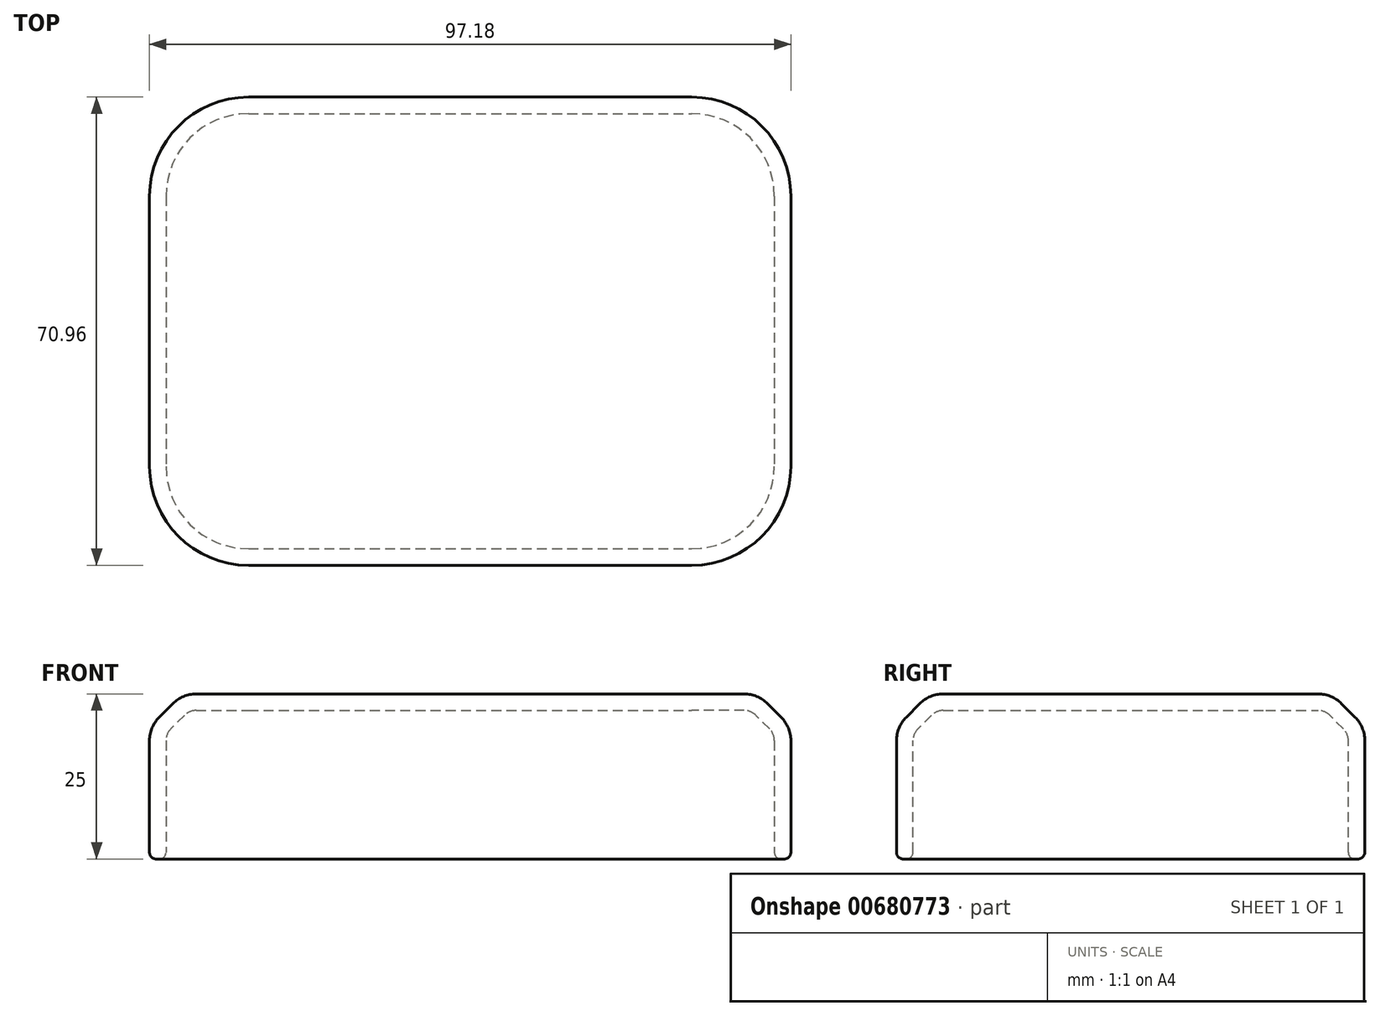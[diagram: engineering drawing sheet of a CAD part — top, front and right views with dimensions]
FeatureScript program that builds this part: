
annotation { "Feature Type Name" : "Feature", "Feature Type Description" : "" }
export const myFeature = defineFeature(function(context is Context, id is Id, definition is map)
    precondition{}
    {
        {
            var Q0;
            Q0=qCreatedBy(makeId("Top.planeOp"),FACE);
            var sketch = newSketch(context, id + "F0", { "sketchPlane" : qUnion([Q0])});
            skLineSegment(sketch, "E0.bottom", {"start": v(-65.06, 47.59) * mm, "end": v(32.12, 47.59) * mm});
            skLineSegment(sketch, "E0.top", {"start": v(-65.06, -23.37) * mm, "end": v(32.12, -23.37) * mm});
            skLineSegment(sketch, "E0.left", {"start": v(-65.06, 47.59) * mm, "end": v(-65.06, -23.37) * mm});
            skLineSegment(sketch, "E0.right", {"start": v(32.12, 47.59) * mm, "end": v(32.12, -23.37) * mm});
            skSolve(sketch);
        }
        {
            var Q0;
            Q0=makeQuery(id+"F0.imprint","IMPRINT",FACE,{"disambiguationData":[TD([[makeQuery(id+"F0.imprint","IMPRINT",EDGE,{"derivedFrom":sQuery(id+"F0.wireOp",EDGE,"E0.bottom")}),-1.0]])]});
            extrude(context, id + "F1", {"entities" : qUnion([Q0]), "depth" : 25 * mm, "offsetDistance" : 25 * mm});
        }
        {
            var Q0;
            Q0=makeQuery(id+"F1.opExtrude","SWEPT_EDGE",EDGE,{"disambiguationData":[OSD([sQuery(id+"F0.wireOp",EDGE,"E0.top"),sQuery(id+"F0.wireOp",EDGE,"E0.left")])]});
            var Q1;
            Q1=makeQuery(id+"F1.opExtrude","SWEPT_EDGE",EDGE,{"disambiguationData":[OSD([sQuery(id+"F0.wireOp",EDGE,"E0.top"),sQuery(id+"F0.wireOp",EDGE,"E0.right")])]});
            var Q2;
            Q2=makeQuery(id+"F1.opExtrude","SWEPT_EDGE",EDGE,{"disambiguationData":[OSD([sQuery(id+"F0.wireOp",EDGE,"E0.bottom"),sQuery(id+"F0.wireOp",EDGE,"E0.right")])]});
            var Q3;
            Q3=makeQuery(id+"F1.opExtrude","SWEPT_EDGE",EDGE,{"disambiguationData":[OSD([sQuery(id+"F0.wireOp",EDGE,"E0.bottom"),sQuery(id+"F0.wireOp",EDGE,"E0.left")])]});
            fillet(context, id + "F2", {"entities" : qUnion([Q0, Q1, Q2, Q3]), "radius" : 15 * mm, "tangentPropagation" : true, "allowEdgeOverflow" : false});
        }
        {
            var Q0;
            Q0=makeQuery(id+"F1.opExtrude","CAP_EDGE",EDGE,{"disambiguationData":[OSD([sQuery(id+"F0.wireOp",EDGE,"E0.left")])],"isStart":false});
            chamfer(context, id + "F3", {"entities" : qUnion([Q0]), "width" : 5 * mm, "tangentPropagation" : true});
        }
        {
            var Q0;
            {var subQ0=sQuery(id+"F0.wireOp",EDGE,"E0.left");Q0=makeQuery(id+"F3.opChamfer","BLEND_EDGE",EDGE,{"blendedFrom":[makeQuery(id+"F1.opExtrude","CAP_EDGE",EDGE,{"disambiguationData":[OSD([subQ0])],"isStart":false}),makeQuery(id+"F1.opExtrude","SWEPT_FACE",FACE,{"disambiguationData":[OSD([subQ0])]})],"blendedInto":[makeQuery(id+"F1.opExtrude","SWEPT_FACE",FACE,{"disambiguationData":[OSD([subQ0])]})]});}
            var Q1;
            {var subQ0=sQuery(id+"F0.wireOp",EDGE,"E0.left");Q1=makeQuery(id+"F3.opChamfer","BLEND_EDGE",EDGE,{"blendedFrom":[makeQuery(id+"F1.opExtrude","CAP_EDGE",EDGE,{"disambiguationData":[OSD([subQ0])],"isStart":false}),makeQuery(id+"F1.opExtrude","CAP_FACE",FACE,{"disambiguationData":[OSD([sQuery(id+"F0.wireOp",EDGE,"E0.bottom"),sQuery(id+"F0.wireOp",EDGE,"E0.top"),subQ0,sQuery(id+"F0.wireOp",EDGE,"E0.right")])],"isStart":false})],"blendedInto":[makeQuery(id+"F1.opExtrude","CAP_FACE",FACE,{"disambiguationData":[OSD([sQuery(id+"F0.wireOp",EDGE,"E0.bottom"),sQuery(id+"F0.wireOp",EDGE,"E0.top"),subQ0,sQuery(id+"F0.wireOp",EDGE,"E0.right")])],"isStart":false})]});}
            fillet(context, id + "F4", {"entities" : qUnion([Q0, Q1]), "radius" : 5 * mm, "tangentPropagation" : true, "allowEdgeOverflow" : false});
        }
        {
            var Q0;
            Q0=makeQuery(id+"F1.opExtrude","CAP_FACE",FACE,{"disambiguationData":[OSD([sQuery(id+"F0.wireOp",EDGE,"E0.bottom"),sQuery(id+"F0.wireOp",EDGE,"E0.top"),sQuery(id+"F0.wireOp",EDGE,"E0.left"),sQuery(id+"F0.wireOp",EDGE,"E0.right")])],"isStart":true});
            shell(context, id + "F5", {"entities" : qUnion([Q0]), "thickness" : 2.5 * mm});
        }
        {
            var Q0;
            {var subQ0=sQuery(id+"F0.wireOp",EDGE,"E0.top");Q0=makeQuery(id+"F5.opShell","OFFSET_EDGE",EDGE,{"disambiguationData":[OSD([subQ0]),TDD([makeQuery(id+"F1.opExtrude","CAP_EDGE",EDGE,{"disambiguationData":[OSD([subQ0])],"isStart":true})])]});}
            var Q1;
            {var subQ0=sQuery(id+"F0.wireOp",EDGE,"E0.left");var subQ1=sQuery(id+"F0.wireOp",EDGE,"E0.top");Q1=makeQuery(id+"F2.opFillet","BLEND_EDGE",EDGE,{"blendedFrom":[makeQuery(id+"F1.opExtrude","SWEPT_EDGE",EDGE,{"disambiguationData":[OSD([subQ1,subQ0])]}),makeQuery(id+"F1.opExtrude","CAP_FACE",FACE,{"disambiguationData":[OSD([sQuery(id+"F0.wireOp",EDGE,"E0.bottom"),subQ1,subQ0,sQuery(id+"F0.wireOp",EDGE,"E0.right")])],"isStart":true})],"blendedInto":[makeQuery(id+"F1.opExtrude","CAP_FACE",FACE,{"disambiguationData":[OSD([sQuery(id+"F0.wireOp",EDGE,"E0.bottom"),subQ1,subQ0,sQuery(id+"F0.wireOp",EDGE,"E0.right")])],"isStart":true})]});}
            fillet(context, id + "F6", {"entities" : qUnion([Q0, Q1]), "radius" : 1 * mm, "tangentPropagation" : true, "allowEdgeOverflow" : false});
        }
    });
